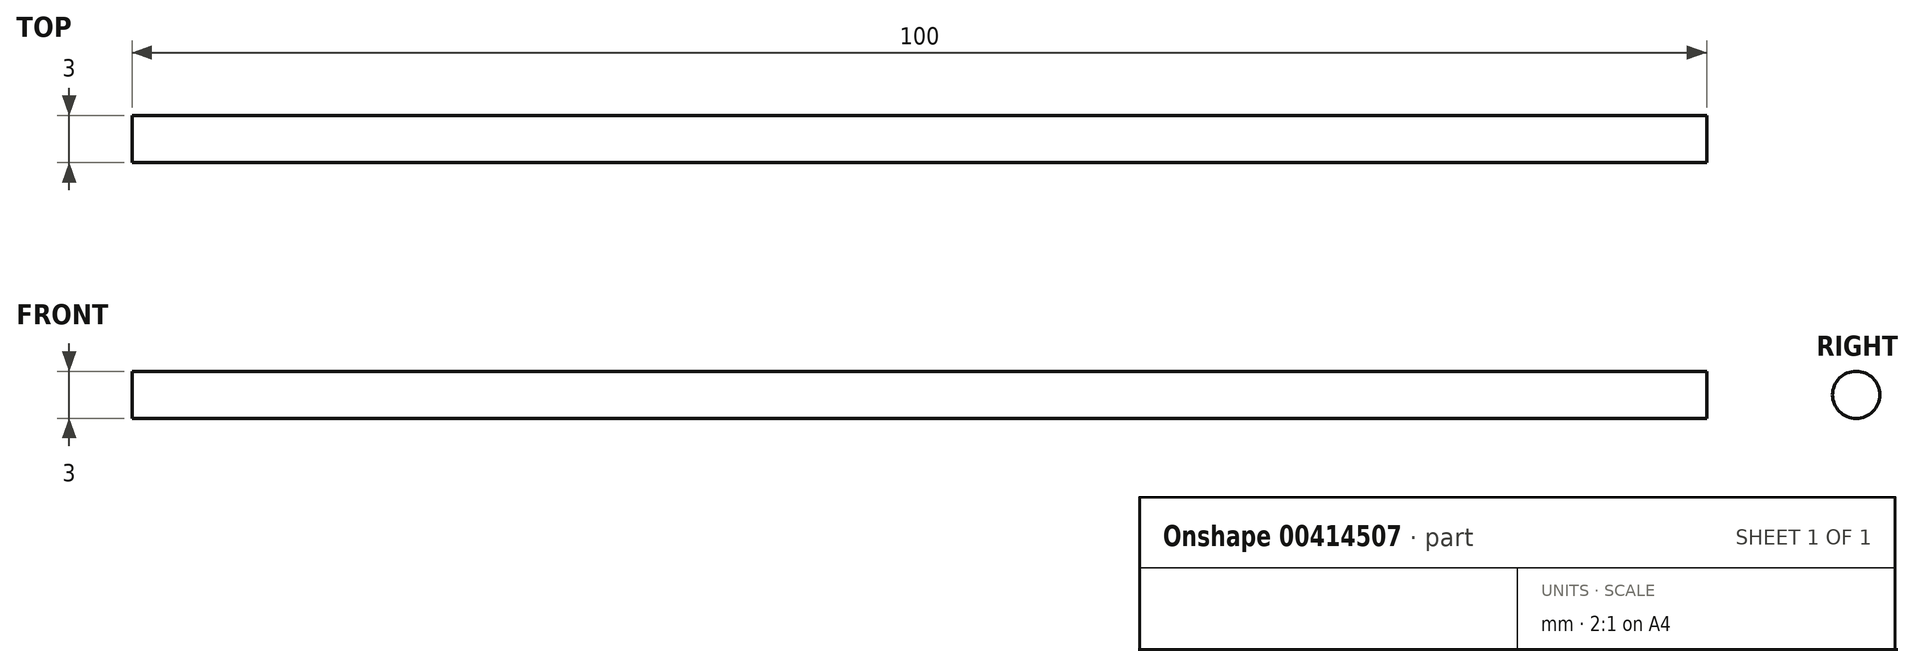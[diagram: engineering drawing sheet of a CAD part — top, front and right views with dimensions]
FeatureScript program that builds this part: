
annotation { "Feature Type Name" : "Feature", "Feature Type Description" : "" }
export const myFeature = defineFeature(function(context is Context, id is Id, definition is map)
    precondition{}
    {
        {
            var Q0;
            Q0=qCreatedBy(makeId("Right.planeOp"),FACE);
            var sketch = newSketch(context, id + "F0", { "sketchPlane" : qUnion([Q0])});
            skCircle(sketch, "E0", {"center": v(0, 0) * mm, "radius": 1.5 * mm});
            skSolve(sketch);
        }
        {
            var Q0;
            Q0 = qSketchRegion(id + "F0", true);
            extrude(context, id + "F1", {"entities" : qUnion([Q0]), "depth" : 100 * mm});
        }
    });
